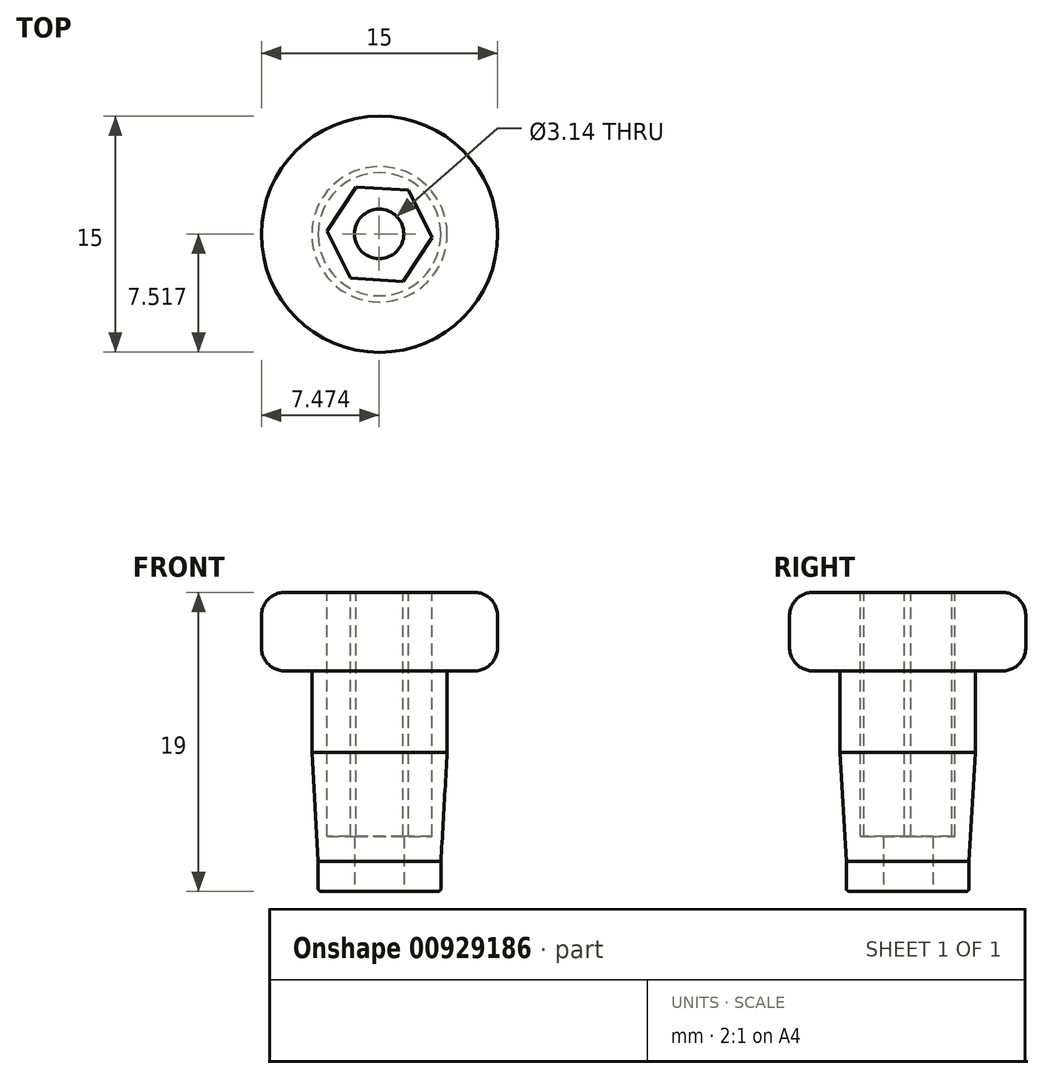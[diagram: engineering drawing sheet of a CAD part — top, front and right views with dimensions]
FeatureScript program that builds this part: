
annotation { "Feature Type Name" : "Feature", "Feature Type Description" : "" }
export const myFeature = defineFeature(function(context is Context, id is Id, definition is map)
    precondition{}
    {
        {
            var Q0;
            Q0=qCreatedBy(makeId("Top.planeOp"),FACE);
            var sketch = newSketch(context, id + "F0", { "sketchPlane" : qUnion([Q0])});
            skCircle(sketch, "E0", {"center": v(-41.47, -26.1) * mm, "radius": 3.9 * mm});
            skSolve(sketch);
        }
        {
            var Q0;
            Q0=qCreatedBy(makeId("Top.planeOp"),FACE);
            var sketch = newSketch(context, id + "F1", { "sketchPlane" : qUnion([Q0])});
            skCircle(sketch, "E1", {"center": v(-41.5, -26.07) * mm, "radius": 1.57 * mm});
            skSolve(sketch);
        }
        {
            var Q0;
            Q0 = qSketchRegion(id + "F0", true);
            extrude(context, id + "F2", {"entities" : qUnion([Q0]), "depth" : 14 * mm, "offsetDistance" : 25 * mm});
        }
        {
            var Q0;
            Q0=makeQuery(id+"F2.opExtrude","CAP_FACE",FACE,{"disambiguationData":[OSD([sQuery(id+"F0.wireOp",EDGE,"E0")])],"isStart":false});
            var sketch = newSketch(context, id + "F3", { "sketchPlane" : qUnion([Q0])});
            skCircle(sketch, "E2", {"center": v(-41.47, -26.1) * mm, "radius": 7.5 * mm});
            skSolve(sketch);
        }
        {
            var Q0;
            Q0 = qSketchRegion(id + "F3", true);
            extrude(context, id + "F4", {"entities" : qUnion([Q0]), "operationType" : NewBodyOperationType.ADD, "depth" : 5 * mm, "offsetDistance" : 25 * mm});
        }
        {
            var Q0;
            Q0=makeQuery(id+"F4.opExtrude","CAP_FACE",FACE,{"disambiguationData":[OSD([sQuery(id+"F3.wireOp",EDGE,"E2")])],"isStart":false});
            var sketch = newSketch(context, id + "F5", { "sketchPlane" : qUnion([Q0])});
            skCircle(sketch, "E3.cCircle", {"center": v(-41.47, -26.1) * mm, "radius": 2.9 * mm, "construction": true});
            skLineSegment(sketch, "E3.0", {"start": v(-38.13, -26.3) * mm, "end": v(-39.98, -29.1) * mm});
            skLineSegment(sketch, "E3.1", {"start": v(-39.98, -29.1) * mm, "end": v(-43.32, -28.89) * mm});
            skLineSegment(sketch, "E3.2", {"start": v(-43.32, -28.89) * mm, "end": v(-44.81, -25.89) * mm});
            skLineSegment(sketch, "E3.3", {"start": v(-44.81, -25.89) * mm, "end": v(-42.97, -23.1) * mm});
            skLineSegment(sketch, "E3.4", {"start": v(-42.97, -23.1) * mm, "end": v(-39.62, -23.3) * mm});
            skLineSegment(sketch, "E3.5", {"start": v(-39.62, -23.3) * mm, "end": v(-38.13, -26.3) * mm});
            skPoint(sketch, "E3.0.midPoint", {"position": v(-39.05, -27.7) * mm});
            skSolve(sketch);
        }
        {
            var Q0;
            {var subQ0=sQuery(id+"F3.wireOp",EDGE,"E2");Q0=makeQuery(id+"F4.boolean.opBoolean","SPLIT",FACE,{"disambiguationData":[TD([makeQuery(id+"F2.opExtrude","SWEPT_FACE",FACE,{"disambiguationData":[OSD([sQuery(id+"F0.wireOp",EDGE,"E0")])]})])],"derivedFrom":makeQuery(id+"F4.opExtrude","CAP_FACE",FACE,{"disambiguationData":[OSD([subQ0])],"isStart":true})});}
            var sketch = newSketch(context, id + "F6", { "sketchPlane" : qUnion([Q0])});
            skCircle(sketch, "E4", {"center": v(-41.47, 26.1) * mm, "radius": 4.3 * mm});
            skSolve(sketch);
        }
        {
            var Q0;
            Q0 = qSketchRegion(id + "F6", true);
            extrude(context, id + "F7", {"entities" : qUnion([Q0]), "operationType" : NewBodyOperationType.ADD, "depth" : 4.1 * mm, "offsetDistance" : 25 * mm});
        }
        {
            var Q0;
            Q0 = qSketchRegion(id + "F1", true);
            extrude(context, id + "F8", {"entities" : qUnion([Q0]), "operationType" : NewBodyOperationType.REMOVE, "depth" : 23.4 * mm, "offsetDistance" : 25 * mm});
        }
        {
            var Q0;
            Q0 = qSketchRegion(id + "F5", true);
            extrude(context, id + "F9", {"entities" : qUnion([Q0]), "operationType" : NewBodyOperationType.REMOVE, "oppositeDirection" : true, "depth" : 15.5 * mm, "offsetDistance" : 25 * mm});
        }
        {
            var Q0;
            Q0=makeQuery(id+"F2.opExtrude","CAP_EDGE",EDGE,{"disambiguationData":[OSD([sQuery(id+"F0.wireOp",EDGE,"E0")])],"isStart":true});
            fillet(context, id + "F10", {"entities" : qUnion([Q0]), "radius" : 0.2 * mm, "tangentPropagation" : true, "allowEdgeOverflow" : false});
        }
        {
            var Q0;
            Q0=makeQuery(id+"F7.boolean.opBoolean","INTERSECT",EDGE,{"derivedFrom":[makeQuery(id+"F2.opExtrude","SWEPT_FACE",FACE,{"disambiguationData":[OSD([sQuery(id+"F0.wireOp",EDGE,"E0")])]}),makeQuery(id+"F7.opExtrude","CAP_FACE",FACE,{"disambiguationData":[OSD([sQuery(id+"F6.wireOp",EDGE,"E4")])],"isStart":false})]});
            chamfer(context, id + "F11", {"entities" : qUnion([Q0]), "chamferType" : ChamferType.OFFSET_ANGLE, "width" : 8 * mm, "oppositeDirection" : false, "angle" : 3.3 * degree, "tangentPropagation" : true});
        }
        {
            var Q0;
            Q0=makeQuery(id+"F4.opExtrude","CAP_EDGE",EDGE,{"disambiguationData":[OSD([sQuery(id+"F3.wireOp",EDGE,"E2")])],"isStart":true});
            fillet(context, id + "F12", {"entities" : qUnion([Q0]), "radius" : 1.5 * mm, "tangentPropagation" : true, "allowEdgeOverflow" : false});
        }
        {
            var Q0;
            Q0=makeQuery(id+"F4.opExtrude","CAP_EDGE",EDGE,{"disambiguationData":[OSD([sQuery(id+"F3.wireOp",EDGE,"E2")])],"isStart":false});
            fillet(context, id + "F13", {"entities" : qUnion([Q0]), "radius" : 1.5 * mm, "tangentPropagation" : true, "allowEdgeOverflow" : false});
        }
    });
